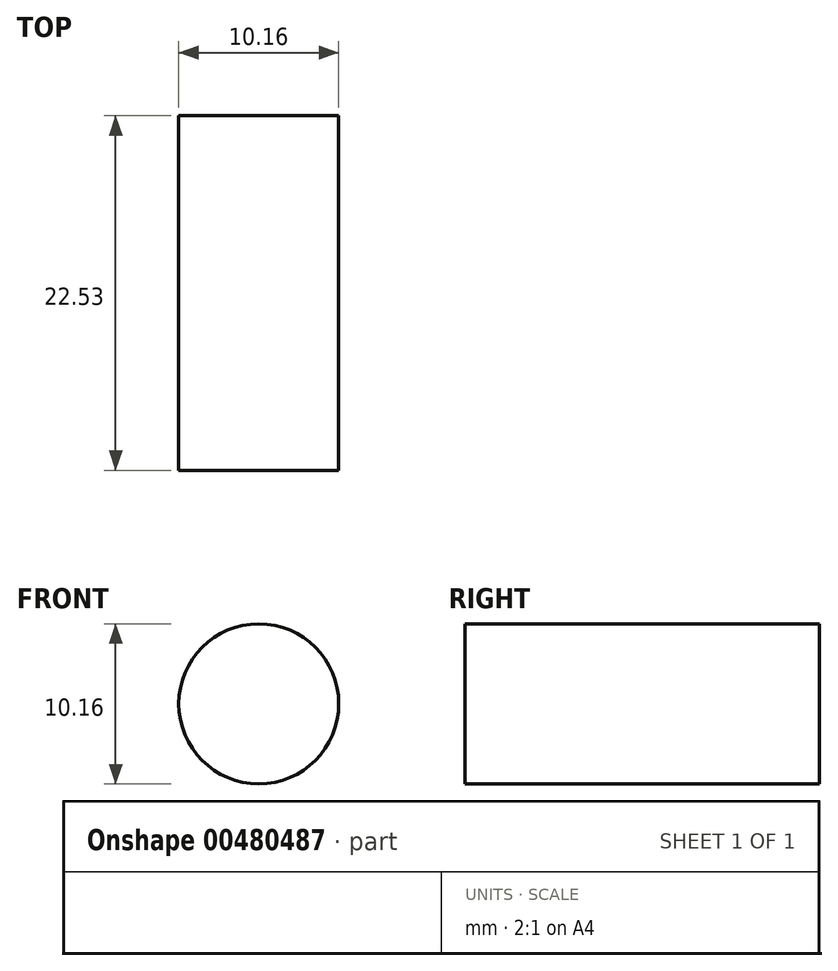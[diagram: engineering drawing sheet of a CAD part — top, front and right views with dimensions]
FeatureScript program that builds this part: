
annotation { "Feature Type Name" : "Feature", "Feature Type Description" : "" }
export const myFeature = defineFeature(function(context is Context, id is Id, definition is map)
    precondition{}
    {
        {
            var Q0;
            Q0=qCreatedBy(makeId("Front.planeOp"),FACE);
            var sketch = newSketch(context, id + "F0", { "sketchPlane" : qUnion([Q0])});
            skCircle(sketch, "E0", {"center": v(0, 0) * mm, "radius": 5.08 * mm});
            skSolve(sketch);
        }
        {
            var Q0;
            Q0 = qSketchRegion(id + "F0", true);
            extrude(context, id + "F1", {"entities" : qUnion([Q0]), "depth" : 22.53 * mm});
        }
    });
